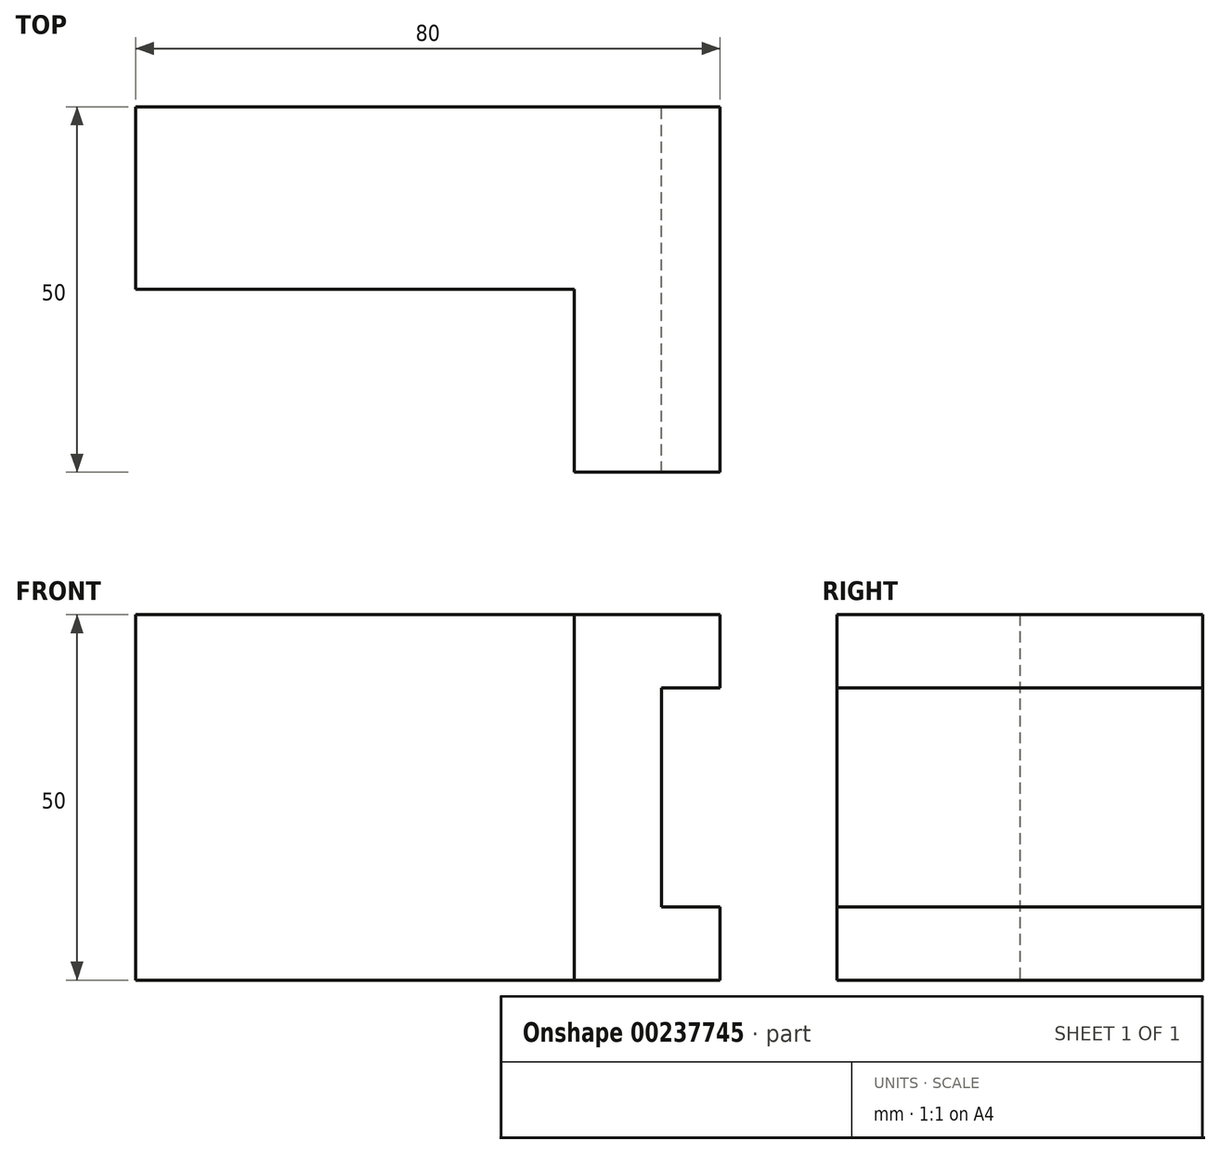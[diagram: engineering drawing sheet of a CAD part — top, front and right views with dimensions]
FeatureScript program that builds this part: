
annotation { "Feature Type Name" : "Feature", "Feature Type Description" : "" }
export const myFeature = defineFeature(function(context is Context, id is Id, definition is map)
    precondition{}
    {
        {
            var Q0;
            Q0=qCreatedBy(makeId("Front.planeOp"),FACE);
            var sketch = newSketch(context, id + "F0", { "sketchPlane" : qUnion([Q0])});
            skLineSegment(sketch, "E0", {"start": v(65.42, -111.87) * mm, "end": v(65.42, -161.87) * mm});
            skLineSegment(sketch, "E1", {"start": v(65.42, -161.87) * mm, "end": v(145.42, -161.87) * mm});
            skLineSegment(sketch, "E2", {"start": v(145.42, -111.87) * mm, "end": v(65.42, -111.87) * mm});
            skLineSegment(sketch, "E3", {"start": v(125.42, -111.87) * mm, "end": v(125.42, -161.87) * mm});
            skLineSegment(sketch, "E4", {"start": v(145.42, -121.87) * mm, "end": v(137.42, -121.87) * mm});
            skLineSegment(sketch, "E5", {"start": v(137.42, -121.87) * mm, "end": v(137.42, -151.87) * mm});
            skLineSegment(sketch, "E6", {"start": v(137.42, -151.87) * mm, "end": v(145.42, -151.87) * mm});
            skLineSegment(sketch, "E7", {"start": v(145.42, -111.87) * mm, "end": v(145.42, -121.87) * mm});
            skLineSegment(sketch, "E8", {"start": v(145.42, -151.87) * mm, "end": v(145.42, -161.87) * mm});
            skSolve(sketch);
        }
        {
            var Q0;
            {var subQ0=sQuery(id+"F0.wireOp",EDGE,"E0");Q0=makeQuery(id+"F0.imprint","IMPRINT",FACE,{"disambiguationData":[TD([[makeQuery(id+"F0.imprint","IMPRINT",EDGE,{"derivedFrom":subQ0}),1.0]])]});}
            extrude(context, id + "F1", {"entities" : qUnion([Q0]), "depth" : 25 * mm});
        }
        {
            var Q0;
            {var subQ0=sQuery(id+"F0.wireOp",EDGE,"E3");Q0=makeQuery(id+"F0.imprint","IMPRINT",FACE,{"disambiguationData":[TD([[makeQuery(id+"F0.imprint","IMPRINT",EDGE,{"derivedFrom":subQ0}),1.0]])]});}
            extrude(context, id + "F2", {"entities" : qUnion([Q0]), "operationType" : NewBodyOperationType.ADD, "depth" : 50 * mm});
        }
    });
